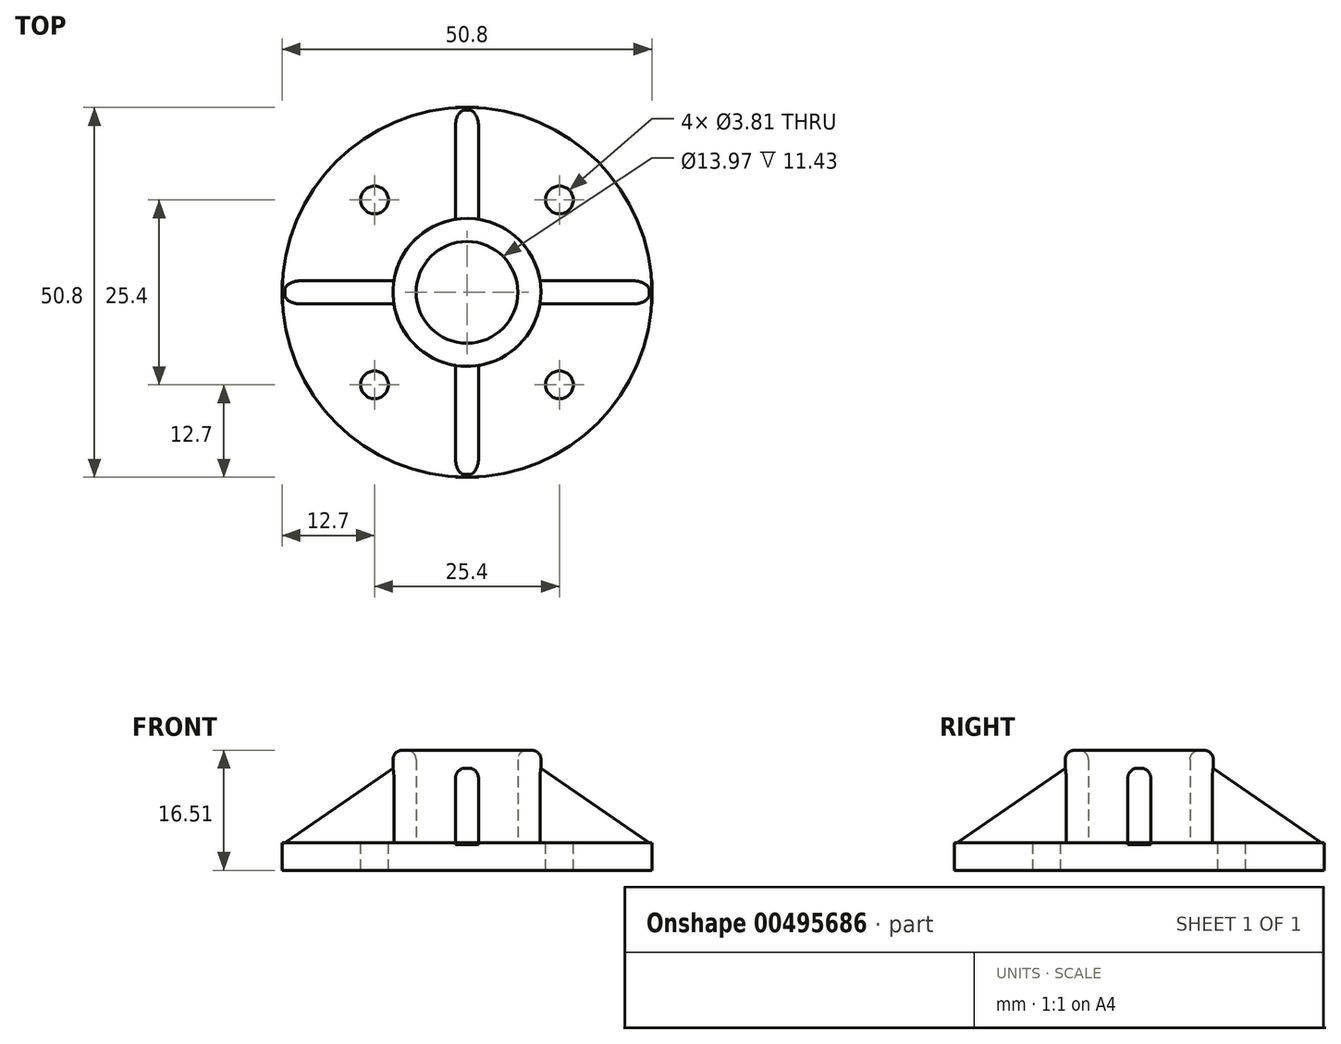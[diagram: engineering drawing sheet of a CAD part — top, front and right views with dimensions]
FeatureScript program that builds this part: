
annotation { "Feature Type Name" : "Feature", "Feature Type Description" : "" }
export const myFeature = defineFeature(function(context is Context, id is Id, definition is map)
    precondition{}
    {
        {
            var Q0;
            Q0=qCreatedBy(makeId("Top.planeOp"),FACE);
            var sketch = newSketch(context, id + "F0", { "sketchPlane" : qUnion([Q0])});
            skCircle(sketch, "E0", {"center": v(0, 0) * mm, "radius": 25.4 * mm});
            skSolve(sketch);
        }
        {
            var Q0;
            Q0=makeQuery(id+"F0.imprint","IMPRINT",FACE,{"disambiguationData":[TD([[makeQuery(id+"F0.imprint","IMPRINT",EDGE,{"derivedFrom":sQuery(id+"F0.wireOp",EDGE,"E0")}),1.0]])]});
            extrude(context, id + "F1", {"entities" : qUnion([Q0]), "depth" : 3.8 * mm});
        }
        {
            var Q0;
            Q0=makeQuery(id+"F1.opExtrude","CAP_FACE",FACE,{"disambiguationData":[OSD([sQuery(id+"F0.wireOp",EDGE,"E0")])],"isStart":false});
            var sketch = newSketch(context, id + "F2", { "sketchPlane" : qUnion([Q0])});
            skCircle(sketch, "E1", {"center": v(0, 0) * mm, "radius": 6.99 * mm});
            skCircle(sketch, "E2", {"center": v(0, 0) * mm, "radius": 10.16 * mm});
            skSolve(sketch);
        }
        {
            var Q0;
            Q0=makeQuery(id+"F2.imprint","IMPRINT",FACE,{"disambiguationData":[TD([[makeQuery(id+"F2.imprint","IMPRINT",EDGE,{"derivedFrom":sQuery(id+"F2.wireOp",EDGE,"E1")}),-1.0]])]});
            extrude(context, id + "F3", {"entities" : qUnion([Q0]), "operationType" : NewBodyOperationType.ADD, "depth" : 12.7 * mm});
        }
        {
            var Q0;
            Q0=qCreatedBy(makeId("Right.planeOp"),FACE);
            var sketch = newSketch(context, id + "F4", { "sketchPlane" : qUnion([Q0])});
            skLineSegment(sketch, "E3.bottom", {"start": v(25.4, 3.56) * mm, "end": v(8.38, 3.56) * mm});
            skLineSegment(sketch, "E3.right", {"start": v(8.38, 3.56) * mm, "end": v(8.38, 15.24) * mm});
            skLineSegment(sketch, "E4", {"start": v(8.38, 15.24) * mm, "end": v(25.4, 3.56) * mm});
            skLineSegment(sketch, "E5.MirrorCS", {"start": v(-8.38, 3.56) * mm, "end": v(-8.38, 15.24) * mm});
            skLineSegment(sketch, "E6.MirrorCS", {"start": v(-25.4, 3.56) * mm, "end": v(-8.38, 3.56) * mm});
            skLineSegment(sketch, "E7.MirrorCS", {"start": v(-8.38, 15.24) * mm, "end": v(-25.4, 3.56) * mm});
            skSolve(sketch);
        }
        {
            var Q0;
            Q0=makeQuery(id+"F4.imprint","IMPRINT",FACE,{"disambiguationData":[TD([[makeQuery(id+"F4.imprint","IMPRINT",EDGE,{"derivedFrom":sQuery(id+"F4.wireOp",EDGE,"E3.bottom")}),-1.0]])]});
            var Q1;
            Q1=makeQuery(id+"F4.imprint","IMPRINT",FACE,{"disambiguationData":[TD([[makeQuery(id+"F4.imprint","IMPRINT",EDGE,{"derivedFrom":sQuery(id+"F4.wireOp",EDGE,"E5.MirrorCS")}),1.0]])]});
            extrude(context, id + "F5", {"entities" : qUnion([Q0, Q1]), "operationType" : NewBodyOperationType.ADD, "endBound" : BoundingType.SYMMETRIC, "depth" : 3.17 * mm});
        }
        {
            var Q0;
            Q0=qCreatedBy(makeId("Front.planeOp"),FACE);
            var sketch = newSketch(context, id + "F6", { "sketchPlane" : qUnion([Q0])});
            skLineSegment(sketch, "E8.bottom", {"start": v(-25.4, 3.56) * mm, "end": v(-8.38, 3.56) * mm});
            skLineSegment(sketch, "E8.right", {"start": v(-8.38, 3.56) * mm, "end": v(-8.38, 15.24) * mm});
            skLineSegment(sketch, "E9", {"start": v(-8.38, 15.24) * mm, "end": v(-25.4, 3.56) * mm});
            skLineSegment(sketch, "E10.MirrorCS", {"start": v(25.4, 3.56) * mm, "end": v(8.38, 3.56) * mm});
            skLineSegment(sketch, "E11.MirrorCS", {"start": v(8.38, 15.24) * mm, "end": v(25.4, 3.56) * mm});
            skLineSegment(sketch, "E12.MirrorCS", {"start": v(8.38, 3.56) * mm, "end": v(8.38, 15.24) * mm});
            skSolve(sketch);
        }
        {
            var Q0;
            Q0=makeQuery(id+"F6.imprint","IMPRINT",FACE,{"disambiguationData":[TD([[makeQuery(id+"F6.imprint","IMPRINT",EDGE,{"derivedFrom":sQuery(id+"F6.wireOp",EDGE,"E8.bottom")}),1.0]])]});
            var Q1;
            Q1=makeQuery(id+"F6.imprint","IMPRINT",FACE,{"disambiguationData":[TD([[makeQuery(id+"F6.imprint","IMPRINT",EDGE,{"derivedFrom":sQuery(id+"F6.wireOp",EDGE,"E10.MirrorCS")}),-1.0]])]});
            extrude(context, id + "F7", {"entities" : qUnion([Q0, Q1]), "operationType" : NewBodyOperationType.ADD, "endBound" : BoundingType.SYMMETRIC, "depth" : 3.17 * mm});
        }
        {
            var Q0;
            Q0=makeQuery(id+"F3.opExtrude","CAP_EDGE",EDGE,{"disambiguationData":[OSD([sQuery(id+"F2.wireOp",EDGE,"E1")])],"isStart":false});
            var Q1;
            Q1=makeQuery(id+"F3.opExtrude","CAP_EDGE",EDGE,{"disambiguationData":[OSD([sQuery(id+"F2.wireOp",EDGE,"E2")])],"isStart":false});
            var Q2;
            {var subQ0=sQuery(id+"F6.wireOp",EDGE,"E9");Q2=makeQuery(id+"F7.boolean.opBoolean","SPLIT",EDGE,{"disambiguationData":[TD([makeQuery(id+"F1.opExtrude","CAP_FACE",FACE,{"disambiguationData":[OSD([sQuery(id+"F0.wireOp",EDGE,"E0")])],"isStart":false})])],"derivedFrom":makeQuery(id+"F7.opExtrude","CAP_EDGE",EDGE,{"disambiguationData":[OSD([subQ0])],"isStart":false})});}
            var Q3;
            {var subQ0=sQuery(id+"F6.wireOp",EDGE,"E9");Q3=makeQuery(id+"F7.boolean.opBoolean","SPLIT",EDGE,{"disambiguationData":[TD([makeQuery(id+"F1.opExtrude","CAP_FACE",FACE,{"disambiguationData":[OSD([sQuery(id+"F0.wireOp",EDGE,"E0")])],"isStart":false})])],"derivedFrom":makeQuery(id+"F7.opExtrude","CAP_EDGE",EDGE,{"disambiguationData":[OSD([subQ0])],"isStart":true})});}
            var Q4;
            {var subQ0=sQuery(id+"F4.wireOp",EDGE,"E7.MirrorCS");Q4=makeQuery(id+"F5.boolean.opBoolean","SPLIT",EDGE,{"disambiguationData":[TD([makeQuery(id+"F1.opExtrude","CAP_FACE",FACE,{"disambiguationData":[OSD([sQuery(id+"F0.wireOp",EDGE,"E0")])],"isStart":false})])],"derivedFrom":makeQuery(id+"F5.opExtrude","CAP_EDGE",EDGE,{"disambiguationData":[OSD([subQ0])],"isStart":true})});}
            var Q5;
            {var subQ0=sQuery(id+"F4.wireOp",EDGE,"E7.MirrorCS");Q5=makeQuery(id+"F5.boolean.opBoolean","SPLIT",EDGE,{"disambiguationData":[TD([makeQuery(id+"F1.opExtrude","CAP_FACE",FACE,{"disambiguationData":[OSD([sQuery(id+"F0.wireOp",EDGE,"E0")])],"isStart":false})])],"derivedFrom":makeQuery(id+"F5.opExtrude","CAP_EDGE",EDGE,{"disambiguationData":[OSD([subQ0])],"isStart":false})});}
            var Q6;
            {var subQ0=sQuery(id+"F6.wireOp",EDGE,"E11.MirrorCS");Q6=makeQuery(id+"F7.boolean.opBoolean","SPLIT",EDGE,{"disambiguationData":[TD([makeQuery(id+"F1.opExtrude","CAP_FACE",FACE,{"disambiguationData":[OSD([sQuery(id+"F0.wireOp",EDGE,"E0")])],"isStart":false})])],"derivedFrom":makeQuery(id+"F7.opExtrude","CAP_EDGE",EDGE,{"disambiguationData":[OSD([subQ0])],"isStart":false})});}
            var Q7;
            {var subQ0=sQuery(id+"F6.wireOp",EDGE,"E11.MirrorCS");Q7=makeQuery(id+"F7.boolean.opBoolean","SPLIT",EDGE,{"disambiguationData":[TD([makeQuery(id+"F1.opExtrude","CAP_FACE",FACE,{"disambiguationData":[OSD([sQuery(id+"F0.wireOp",EDGE,"E0")])],"isStart":false})])],"derivedFrom":makeQuery(id+"F7.opExtrude","CAP_EDGE",EDGE,{"disambiguationData":[OSD([subQ0])],"isStart":true})});}
            var Q8;
            {var subQ0=sQuery(id+"F4.wireOp",EDGE,"E4");Q8=makeQuery(id+"F5.boolean.opBoolean","SPLIT",EDGE,{"disambiguationData":[TD([makeQuery(id+"F1.opExtrude","CAP_FACE",FACE,{"disambiguationData":[OSD([sQuery(id+"F0.wireOp",EDGE,"E0")])],"isStart":false})])],"derivedFrom":makeQuery(id+"F5.opExtrude","CAP_EDGE",EDGE,{"disambiguationData":[OSD([subQ0])],"isStart":false})});}
            var Q9;
            {var subQ0=sQuery(id+"F4.wireOp",EDGE,"E4");Q9=makeQuery(id+"F5.boolean.opBoolean","SPLIT",EDGE,{"disambiguationData":[TD([makeQuery(id+"F1.opExtrude","CAP_FACE",FACE,{"disambiguationData":[OSD([sQuery(id+"F0.wireOp",EDGE,"E0")])],"isStart":false})])],"derivedFrom":makeQuery(id+"F5.opExtrude","CAP_EDGE",EDGE,{"disambiguationData":[OSD([subQ0])],"isStart":true})});}
            fillet(context, id + "F8", {"entities" : qUnion([Q0, Q1, Q2, Q3, Q4, Q5, Q6, Q7, Q8, Q9]), "radius" : 1.27 * mm, "tangentPropagation" : true, "allowEdgeOverflow" : false});
        }
        {
            var Q0;
            {var subQ0=sQuery(id+"F0.wireOp",EDGE,"E0");Q0=makeQuery(id+"F3.boolean.opBoolean","SPLIT",FACE,{"disambiguationData":[TD([makeQuery(id+"F1.opExtrude","SWEPT_FACE",FACE,{"disambiguationData":[OSD([subQ0])]})])],"derivedFrom":makeQuery(id+"F1.opExtrude","CAP_FACE",FACE,{"disambiguationData":[OSD([subQ0])],"isStart":false})});}
            var sketch = newSketch(context, id + "F9", { "sketchPlane" : qUnion([Q0])});
            skCircle(sketch, "E13", {"center": v(-12.7, 12.7) * mm, "radius": 1.9 * mm});
            skCircle(sketch, "E14.1.0", {"center": v(12.7, 12.7) * mm, "radius": 1.9 * mm});
            skCircle(sketch, "E14.2.0", {"center": v(12.7, -12.7) * mm, "radius": 1.9 * mm});
            skCircle(sketch, "E14.3.0", {"center": v(-12.7, -12.7) * mm, "radius": 1.9 * mm});
            skPoint(sketch, "E14.center", {"position": v(0, 0) * mm});
            skLineSegment(sketch, "E14.anchor1", {"start": v(0, 0) * mm, "end": v(-12.7, 12.7) * mm, "construction": true});
            skLineSegment(sketch, "E14.anchor2", {"start": v(0, 0) * mm, "end": v(-12.7, -12.7) * mm, "construction": true});
            skSolve(sketch);
        }
        {
            var Q0;
            Q0=makeQuery(id+"F9.imprint","IMPRINT",FACE,{"disambiguationData":[TD([[makeQuery(id+"F9.imprint","IMPRINT",EDGE,{"derivedFrom":sQuery(id+"F9.wireOp",EDGE,"E13")}),1.0]])]});
            var Q1;
            Q1=makeQuery(id+"F9.imprint","IMPRINT",FACE,{"disambiguationData":[TD([[makeQuery(id+"F9.imprint","IMPRINT",EDGE,{"derivedFrom":sQuery(id+"F9.wireOp",EDGE,"E14.1.0")}),1.0]])]});
            var Q2;
            Q2=makeQuery(id+"F9.imprint","IMPRINT",FACE,{"disambiguationData":[TD([[makeQuery(id+"F9.imprint","IMPRINT",EDGE,{"derivedFrom":sQuery(id+"F9.wireOp",EDGE,"E14.2.0")}),1.0]])]});
            var Q3;
            Q3=makeQuery(id+"F9.imprint","IMPRINT",FACE,{"disambiguationData":[TD([[makeQuery(id+"F9.imprint","IMPRINT",EDGE,{"derivedFrom":sQuery(id+"F9.wireOp",EDGE,"E14.3.0")}),1.0]])]});
            var Q4;
            Q4=makeQuery(id+"F1.opExtrude","CAP_FACE",FACE,{"disambiguationData":[OSD([sQuery(id+"F0.wireOp",EDGE,"E0")])],"isStart":true});
            extrude(context, id + "F10", {"entities" : qUnion([Q0, Q1, Q2, Q3]), "operationType" : NewBodyOperationType.REMOVE, "endBound" : BoundingType.UP_TO_SURFACE, "oppositeDirection" : true, "endBoundEntityFace" : qUnion([Q4]), "depth" : 25.4 * mm});
        }
    });
